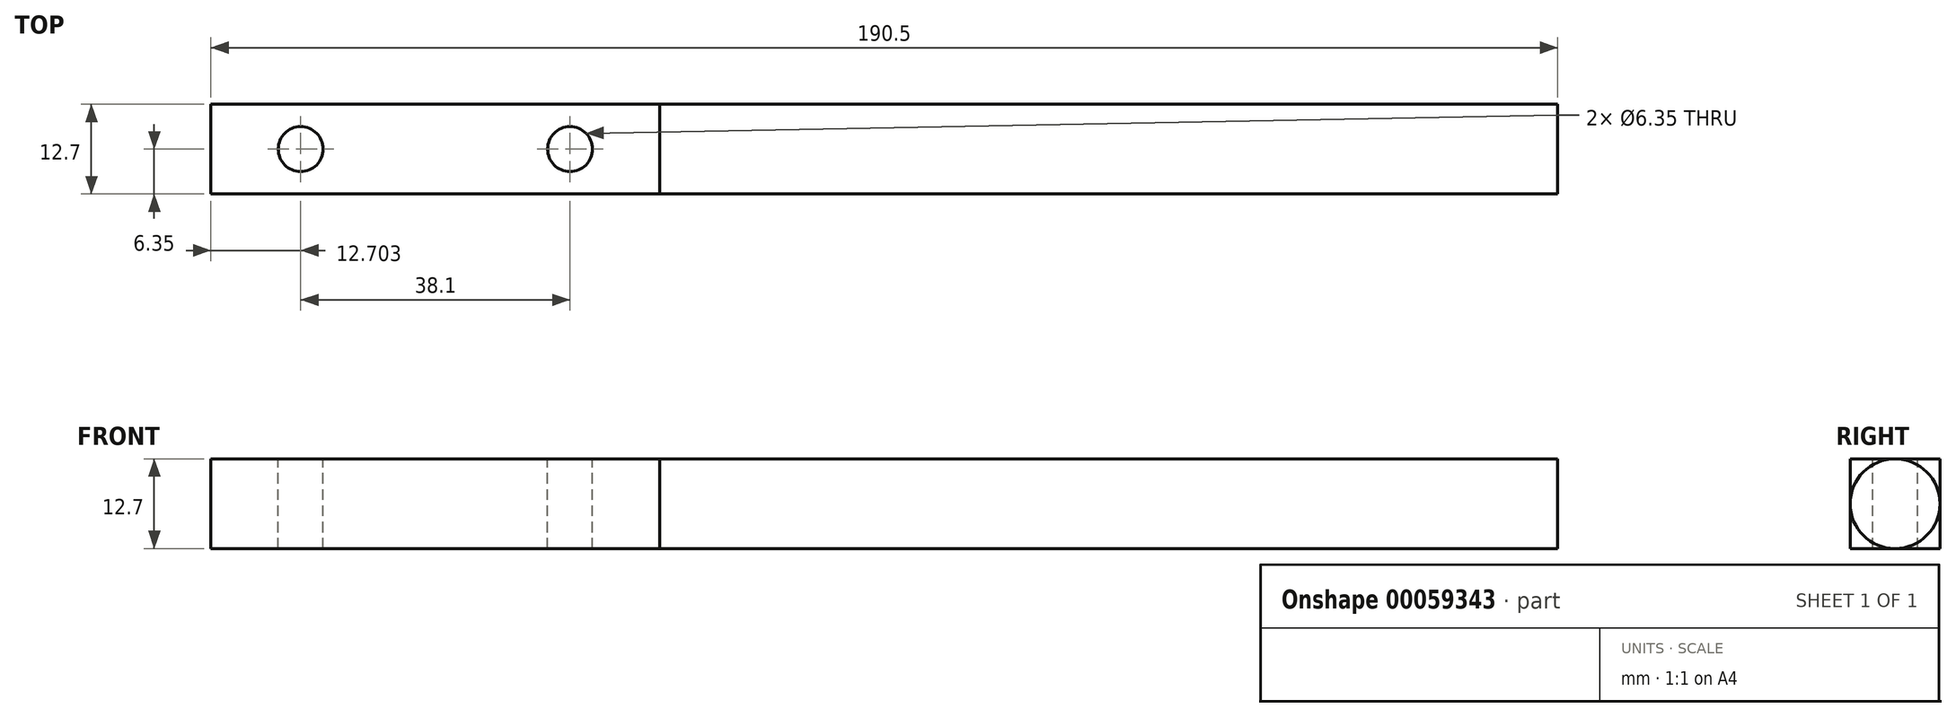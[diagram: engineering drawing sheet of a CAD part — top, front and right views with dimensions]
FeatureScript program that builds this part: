
annotation { "Feature Type Name" : "Feature", "Feature Type Description" : "" }
export const myFeature = defineFeature(function(context is Context, id is Id, definition is map)
    precondition{}
    {
        {
            var Q0;
            Q0=qCreatedBy(makeId("Top.planeOp"),FACE);
            var sketch = newSketch(context, id + "F0", { "sketchPlane" : qUnion([Q0])});
            skLineSegment(sketch, "E0.bottom", {"start": v(-57.72, 6.35) * mm, "end": v(69.28, 6.35) * mm});
            skLineSegment(sketch, "E0.left", {"start": v(-57.72, 6.35) * mm, "end": v(-57.72, 0) * mm});
            skPoint(sketch, "E1", {"position": v(-57.72, 0) * mm});
            skPoint(sketch, "E2", {"position": v(0, 0) * mm});
            skPoint(sketch, "E3", {"position": v(69.28, 0) * mm});
            skLineSegment(sketch, "E4", {"start": v(69.28, 6.35) * mm, "end": v(69.28, 0) * mm});
            skLineSegment(sketch, "E5", {"start": v(69.28, 0) * mm, "end": v(-57.72, 0) * mm});
            skSolve(sketch);
        }
        {
            var Q0;
            Q0=makeQuery(id+"F0.imprint","IMPRINT",FACE,{"disambiguationData":[TD([[makeQuery(id+"F0.imprint","IMPRINT",EDGE,{"derivedFrom":sQuery(id+"F0.wireOp",EDGE,"E0.bottom")}),-1.0]])]});
            var Q1;
            Q1=sQuery(id+"F0.wireOp",EDGE,"E5");
            revolve(context, id + "F1", {"entities" : qUnion([Q0]), "axis" : qUnion([Q1]), "revolveType" : RevolveType.FULL});
        }
        {
            var Q0;
            Q0=makeQuery(id+"F1.opRevolve","SWEPT_FACE",FACE,{"disambiguationData":[OSD([sQuery(id+"F0.wireOp",EDGE,"E0.left")])]});
            var sketch = newSketch(context, id + "F2", { "sketchPlane" : qUnion([Q0])});
            skLineSegment(sketch, "E6.bottom", {"start": v(-6.35, 6.35) * mm, "end": v(6.35, 6.35) * mm});
            skLineSegment(sketch, "E6.top", {"start": v(-6.35, -6.35) * mm, "end": v(6.35, -6.35) * mm});
            skLineSegment(sketch, "E6.left", {"start": v(-6.35, 6.35) * mm, "end": v(-6.35, -6.35) * mm});
            skLineSegment(sketch, "E6.right", {"start": v(6.35, 6.35) * mm, "end": v(6.35, -6.35) * mm});
            skSolve(sketch);
        }
        {
            var Q0;
            {var subQ0=sQuery(id+"F2.wireOp",EDGE,"E6.right");var subQ1=sQuery(id+"F2.wireOp",EDGE,"E6.bottom");var subQ2=makeQuery(id+"F2.imprint","INTERSECT",VERTEX,{"derivedFrom":[subQ1,subQ0]});Q0=makeQuery(id+"F2.imprint","IMPRINT",FACE,{"disambiguationData":[TD([[makeQuery(id+"F2.imprint","IMPRINT",EDGE,{"disambiguationData":[TD([[subQ2,1.0]])],"derivedFrom":subQ1}),-1.0]])]});}
            var Q1;
            {var subQ0=sQuery(id+"F2.wireOp",EDGE,"E6.left");var subQ1=sQuery(id+"F2.wireOp",EDGE,"E6.bottom");var subQ2=makeQuery(id+"F2.imprint","INTERSECT",VERTEX,{"derivedFrom":[subQ1,subQ0]});Q1=makeQuery(id+"F2.imprint","IMPRINT",FACE,{"disambiguationData":[TD([[makeQuery(id+"F2.imprint","IMPRINT",EDGE,{"disambiguationData":[TD([[subQ2,-1.0]])],"derivedFrom":subQ1}),-1.0]])]});}
            var Q2;
            {var subQ0=sQuery(id+"F2.wireOp",EDGE,"E6.right");var subQ1=sQuery(id+"F2.wireOp",EDGE,"E6.top");var subQ2=makeQuery(id+"F2.imprint","INTERSECT",VERTEX,{"derivedFrom":[subQ1,subQ0]});Q2=makeQuery(id+"F2.imprint","IMPRINT",FACE,{"disambiguationData":[TD([[makeQuery(id+"F2.imprint","IMPRINT",EDGE,{"disambiguationData":[TD([[subQ2,1.0]])],"derivedFrom":subQ1}),1.0]])]});}
            var Q3;
            {var subQ0=makeQuery(id+"F1.opRevolve","SWEPT_EDGE",EDGE,{"disambiguationData":[OSD([sQuery(id+"F0.wireOp",EDGE,"E0.bottom"),sQuery(id+"F0.wireOp",EDGE,"E0.left")])]});var subQ1=makeQuery(id+"F2.imprint","INTERSECT",VERTEX,{"derivedFrom":[subQ0,sQuery(id+"F2.wireOp",EDGE,"E6.bottom")]});Q3=makeQuery(id+"F2.imprint","IMPRINT",FACE,{"disambiguationData":[TD([[makeQuery(id+"F2.imprint","IMPRINT",EDGE,{"disambiguationData":[TD([[subQ1,1.0]])],"derivedFrom":subQ0}),-1.0]])]});}
            var Q4;
            {var subQ0=sQuery(id+"F2.wireOp",EDGE,"E6.left");var subQ1=sQuery(id+"F2.wireOp",EDGE,"E6.top");var subQ2=makeQuery(id+"F2.imprint","INTERSECT",VERTEX,{"derivedFrom":[subQ1,subQ0]});Q4=makeQuery(id+"F2.imprint","IMPRINT",FACE,{"disambiguationData":[TD([[makeQuery(id+"F2.imprint","IMPRINT",EDGE,{"disambiguationData":[TD([[subQ2,-1.0]])],"derivedFrom":subQ1}),1.0]])]});}
            extrude(context, id + "F3", {"entities" : qUnion([Q0, Q1, Q2, Q3, Q4]), "operationType" : NewBodyOperationType.ADD, "depth" : 63.5 * mm});
        }
        {
            var Q0;
            Q0=makeQuery(id+"F3.opExtrude","SWEPT_FACE",FACE,{"disambiguationData":[OSD([sQuery(id+"F2.wireOp",EDGE,"E6.bottom")])]});
            var sketch = newSketch(context, id + "F4", { "sketchPlane" : qUnion([Q0])});
            skCircle(sketch, "E7", {"center": v(-70.42, 0) * mm, "radius": 3.18 * mm});
            skCircle(sketch, "E8", {"center": v(-108.52, 0) * mm, "radius": 3.18 * mm});
            skSolve(sketch);
        }
        {
            var Q0;
            Q0 = qSketchRegion(id + "F4", true);
            extrude(context, id + "F5", {"entities" : qUnion([Q0]), "operationType" : NewBodyOperationType.REMOVE, "oppositeDirection" : true, "depth" : 25.4 * mm});
        }
    });
